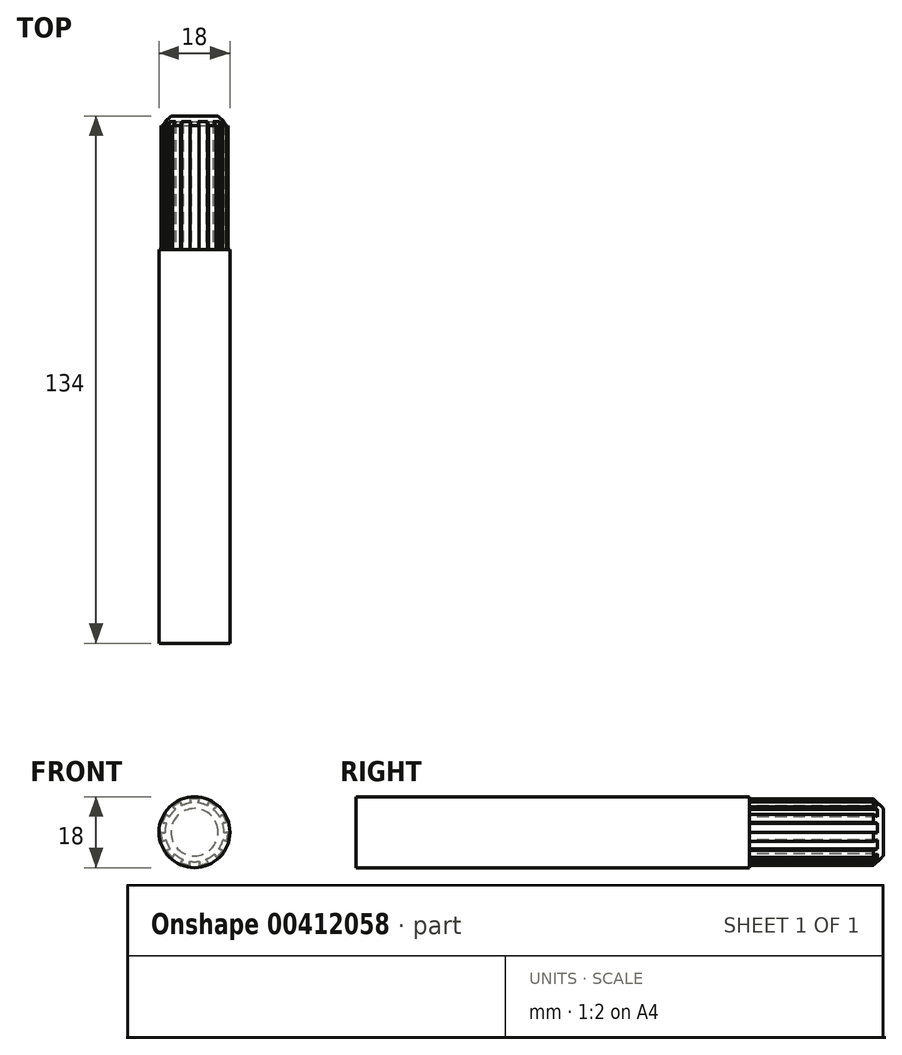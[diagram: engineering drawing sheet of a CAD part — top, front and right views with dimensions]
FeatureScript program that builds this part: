
annotation { "Feature Type Name" : "Feature", "Feature Type Description" : "" }
export const myFeature = defineFeature(function(context is Context, id is Id, definition is map)
    precondition{}
    {
        {
            var Q0;
            Q0=qCreatedBy(makeId("Front.planeOp"),FACE);
            var sketch = newSketch(context, id + "F0", { "sketchPlane" : qUnion([Q0])});
            skCircle(sketch, "E0", {"center": v(0, 0) * mm, "radius": 9 * mm});
            skSolve(sketch);
        }
        {
            var Q0;
            Q0=makeQuery(id+"F0.imprint","IMPRINT",FACE,{"disambiguationData":[TD([[makeQuery(id+"F0.imprint","IMPRINT",EDGE,{"derivedFrom":sQuery(id+"F0.wireOp",EDGE,"E0")}),1.0]])]});
            extrude(context, id + "F1", {"entities" : qUnion([Q0]), "depth" : 100 * mm});
        }
        {
            var Q0;
            Q0=qCreatedBy(makeId("Front.planeOp"),FACE);
            var sketch = newSketch(context, id + "F2", { "sketchPlane" : qUnion([Q0])});
            skCircle(sketch, "E1", {"center": v(0, 0) * mm, "radius": 8.5 * mm});
            skCircle(sketch, "E2", {"center": v(0, 0) * mm, "radius": 7.5 * mm});
            skLineSegment(sketch, "E3", {"start": v(0, 14.32) * mm, "end": v(0, -11.4) * mm, "construction": true});
            skPoint(sketch, "E4", {"position": v(-0.88, 7.45) * mm});
            skPoint(sketch, "E5", {"position": v(0.88, 7.45) * mm});
            skPoint(sketch, "E6", {"position": v(-1.17, 8.42) * mm});
            skPoint(sketch, "E7", {"position": v(1.17, 8.42) * mm});
            skLineSegment(sketch, "E8", {"start": v(0.88, 7.45) * mm, "end": v(1.17, 8.42) * mm});
            skLineSegment(sketch, "E9", {"start": v(-0.88, 7.45) * mm, "end": v(-1.17, 8.42) * mm});
            skPoint(sketch, "E10.1.0", {"position": v(-3.28, 6.74) * mm});
            skPoint(sketch, "E10.1.1", {"position": v(-5.54, 6.45) * mm});
            skLineSegment(sketch, "E10.1.2", {"start": v(-3.28, 6.74) * mm, "end": v(-3.57, 7.71) * mm});
            skPoint(sketch, "E10.1.3", {"position": v(-3.57, 7.71) * mm});
            skPoint(sketch, "E10.1.4", {"position": v(-4.77, 5.79) * mm});
            skLineSegment(sketch, "E10.1.5", {"start": v(-4.77, 5.79) * mm, "end": v(-5.54, 6.45) * mm});
            skPoint(sketch, "E10.2.0", {"position": v(-6.4, 3.9) * mm});
            skPoint(sketch, "E10.2.1", {"position": v(-8.14, 2.43) * mm});
            skLineSegment(sketch, "E10.2.2", {"start": v(-6.4, 3.9) * mm, "end": v(-7.17, 4.56) * mm});
            skPoint(sketch, "E10.2.3", {"position": v(-7.17, 4.56) * mm});
            skPoint(sketch, "E10.2.4", {"position": v(-7.14, 2.29) * mm});
            skLineSegment(sketch, "E10.2.5", {"start": v(-7.14, 2.29) * mm, "end": v(-8.14, 2.43) * mm});
            skPoint(sketch, "E10.3.0", {"position": v(-7.5, -0.18) * mm});
            skPoint(sketch, "E10.3.1", {"position": v(-8.17, -2.36) * mm});
            skLineSegment(sketch, "E10.3.2", {"start": v(-7.5, -0.18) * mm, "end": v(-8.5, -0.04) * mm});
            skPoint(sketch, "E10.3.3", {"position": v(-8.5, -0.04) * mm});
            skPoint(sketch, "E10.3.4", {"position": v(-7.25, -1.93) * mm});
            skLineSegment(sketch, "E10.3.5", {"start": v(-7.25, -1.93) * mm, "end": v(-8.17, -2.36) * mm});
            skPoint(sketch, "E10.4.0", {"position": v(-6.2, -4.2) * mm});
            skPoint(sketch, "E10.4.1", {"position": v(-5.6, -6.4) * mm});
            skLineSegment(sketch, "E10.4.2", {"start": v(-6.2, -4.2) * mm, "end": v(-7.13, -4.63) * mm});
            skPoint(sketch, "E10.4.3", {"position": v(-7.13, -4.63) * mm});
            skPoint(sketch, "E10.4.4", {"position": v(-5.05, -5.55) * mm});
            skLineSegment(sketch, "E10.4.5", {"start": v(-5.05, -5.55) * mm, "end": v(-5.6, -6.4) * mm});
            skPoint(sketch, "E10.5.0", {"position": v(-2.95, -6.9) * mm});
            skPoint(sketch, "E10.5.1", {"position": v(-1.25, -8.4) * mm});
            skLineSegment(sketch, "E10.5.2", {"start": v(-2.95, -6.9) * mm, "end": v(-3.5, -7.75) * mm});
            skPoint(sketch, "E10.5.3", {"position": v(-3.5, -7.75) * mm});
            skPoint(sketch, "E10.5.4", {"position": v(-1.25, -7.4) * mm});
            skLineSegment(sketch, "E10.5.5", {"start": v(-1.25, -7.4) * mm, "end": v(-1.25, -8.4) * mm});
            skPoint(sketch, "E10.6.0", {"position": v(1.25, -7.4) * mm});
            skPoint(sketch, "E10.6.1", {"position": v(3.5, -7.75) * mm});
            skLineSegment(sketch, "E10.6.2", {"start": v(1.25, -7.4) * mm, "end": v(1.25, -8.4) * mm});
            skPoint(sketch, "E10.6.3", {"position": v(1.25, -8.4) * mm});
            skPoint(sketch, "E10.6.4", {"position": v(2.95, -6.9) * mm});
            skLineSegment(sketch, "E10.6.5", {"start": v(2.95, -6.9) * mm, "end": v(3.5, -7.75) * mm});
            skPoint(sketch, "E10.7.0", {"position": v(5.05, -5.55) * mm});
            skPoint(sketch, "E10.7.1", {"position": v(7.13, -4.63) * mm});
            skLineSegment(sketch, "E10.7.2", {"start": v(5.05, -5.55) * mm, "end": v(5.6, -6.4) * mm});
            skPoint(sketch, "E10.7.3", {"position": v(5.6, -6.4) * mm});
            skPoint(sketch, "E10.7.4", {"position": v(6.2, -4.2) * mm});
            skLineSegment(sketch, "E10.7.5", {"start": v(6.2, -4.2) * mm, "end": v(7.13, -4.63) * mm});
            skPoint(sketch, "E10.8.0", {"position": v(7.25, -1.93) * mm});
            skPoint(sketch, "E10.8.1", {"position": v(8.5, -0.04) * mm});
            skLineSegment(sketch, "E10.8.2", {"start": v(7.25, -1.93) * mm, "end": v(8.17, -2.36) * mm});
            skPoint(sketch, "E10.8.3", {"position": v(8.17, -2.36) * mm});
            skPoint(sketch, "E10.8.4", {"position": v(7.5, -0.18) * mm});
            skLineSegment(sketch, "E10.8.5", {"start": v(7.5, -0.18) * mm, "end": v(8.5, -0.04) * mm});
            skPoint(sketch, "E10.9.0", {"position": v(7.14, 2.29) * mm});
            skPoint(sketch, "E10.9.1", {"position": v(7.17, 4.56) * mm});
            skLineSegment(sketch, "E10.9.2", {"start": v(7.14, 2.29) * mm, "end": v(8.14, 2.43) * mm});
            skPoint(sketch, "E10.9.3", {"position": v(8.14, 2.43) * mm});
            skPoint(sketch, "E10.9.4", {"position": v(6.4, 3.9) * mm});
            skLineSegment(sketch, "E10.9.5", {"start": v(6.4, 3.9) * mm, "end": v(7.17, 4.56) * mm});
            skPoint(sketch, "E10.10.0", {"position": v(4.77, 5.79) * mm});
            skPoint(sketch, "E10.10.1", {"position": v(3.57, 7.71) * mm});
            skLineSegment(sketch, "E10.10.2", {"start": v(4.77, 5.79) * mm, "end": v(5.54, 6.45) * mm});
            skPoint(sketch, "E10.10.3", {"position": v(5.54, 6.45) * mm});
            skPoint(sketch, "E10.10.4", {"position": v(3.28, 6.74) * mm});
            skLineSegment(sketch, "E10.10.5", {"start": v(3.28, 6.74) * mm, "end": v(3.57, 7.71) * mm});
            skSolve(sketch);
        }
        {
            var Q0;
            Q0 = qSketchRegion(id + "F2", true);
            var Q1;
            {var subQ0=sQuery(id+"F2.wireOp",EDGE,"E2");var subQ8=makeQuery(id+"F2.imprint","INTERSECT",VERTEX,{"derivedFrom":[subQ0,sQuery(id+"F2.wireOp",EDGE,"E10.9.2")]});Q1=makeQuery(id+"F2.imprint","IMPRINT",FACE,{"disambiguationData":[TD([[makeQuery(id+"F2.imprint","IMPRINT",EDGE,{"disambiguationData":[TD([[subQ8,-1.0]])],"derivedFrom":subQ0}),1.0]])]});}
            extrude(context, id + "F3", {"entities" : qUnion([Q0, Q1]), "operationType" : NewBodyOperationType.ADD, "oppositeDirection" : true, "depth" : 34 * mm});
        }
        {
            var Q0;
            Q0=makeQuery(id+"F3.opExtrude","CAP_EDGE",EDGE,{"disambiguationData":[OSD([sQuery(id+"F2.wireOp",EDGE,"E1")])],"isStart":false});
            chamfer(context, id + "F4", {"entities" : qUnion([Q0]), "width" : 2.5 * mm, "tangentPropagation" : true});
        }
        {
            var Q0;
            {var subQ0=sQuery(id+"F2.wireOp",EDGE,"E10.4.5");Q0=makeQuery(id+"F2.imprint","IMPRINT",FACE,{"disambiguationData":[TD([[makeQuery(id+"F2.imprint","IMPRINT",EDGE,{"derivedFrom":subQ0}),1.0]])]});}
            var Q1;
            {var subQ0=sQuery(id+"F2.wireOp",EDGE,"E10.3.5");Q1=makeQuery(id+"F2.imprint","IMPRINT",FACE,{"disambiguationData":[TD([[makeQuery(id+"F2.imprint","IMPRINT",EDGE,{"derivedFrom":subQ0}),1.0]])]});}
            var Q2;
            {var subQ0=sQuery(id+"F2.wireOp",EDGE,"E10.2.5");Q2=makeQuery(id+"F2.imprint","IMPRINT",FACE,{"disambiguationData":[TD([[makeQuery(id+"F2.imprint","IMPRINT",EDGE,{"derivedFrom":subQ0}),1.0]])]});}
            var Q3;
            {var subQ0=sQuery(id+"F2.wireOp",EDGE,"E10.1.5");Q3=makeQuery(id+"F2.imprint","IMPRINT",FACE,{"disambiguationData":[TD([[makeQuery(id+"F2.imprint","IMPRINT",EDGE,{"derivedFrom":subQ0}),1.0]])]});}
            var Q4;
            {var subQ0=sQuery(id+"F2.wireOp",EDGE,"E9");Q4=makeQuery(id+"F2.imprint","IMPRINT",FACE,{"disambiguationData":[TD([[makeQuery(id+"F2.imprint","IMPRINT",EDGE,{"derivedFrom":subQ0}),1.0]])]});}
            var Q5;
            {var subQ0=sQuery(id+"F2.wireOp",EDGE,"E8");Q5=makeQuery(id+"F2.imprint","IMPRINT",FACE,{"disambiguationData":[TD([[makeQuery(id+"F2.imprint","IMPRINT",EDGE,{"derivedFrom":subQ0}),-1.0]])]});}
            var Q6;
            {var subQ0=sQuery(id+"F2.wireOp",EDGE,"E10.9.5");Q6=makeQuery(id+"F2.imprint","IMPRINT",FACE,{"disambiguationData":[TD([[makeQuery(id+"F2.imprint","IMPRINT",EDGE,{"derivedFrom":subQ0}),1.0]])]});}
            var Q7;
            {var subQ0=sQuery(id+"F2.wireOp",EDGE,"E10.8.5");Q7=makeQuery(id+"F2.imprint","IMPRINT",FACE,{"disambiguationData":[TD([[makeQuery(id+"F2.imprint","IMPRINT",EDGE,{"derivedFrom":subQ0}),1.0]])]});}
            var Q8;
            {var subQ0=sQuery(id+"F2.wireOp",EDGE,"E10.7.5");Q8=makeQuery(id+"F2.imprint","IMPRINT",FACE,{"disambiguationData":[TD([[makeQuery(id+"F2.imprint","IMPRINT",EDGE,{"derivedFrom":subQ0}),1.0]])]});}
            var Q9;
            {var subQ0=sQuery(id+"F2.wireOp",EDGE,"E10.6.5");Q9=makeQuery(id+"F2.imprint","IMPRINT",FACE,{"disambiguationData":[TD([[makeQuery(id+"F2.imprint","IMPRINT",EDGE,{"derivedFrom":subQ0}),1.0]])]});}
            var Q10;
            {var subQ0=sQuery(id+"F2.wireOp",EDGE,"E10.5.5");Q10=makeQuery(id+"F2.imprint","IMPRINT",FACE,{"disambiguationData":[TD([[makeQuery(id+"F2.imprint","IMPRINT",EDGE,{"derivedFrom":subQ0}),1.0]])]});}
            extrude(context, id + "F5", {"entities" : qUnion([Q0, Q1, Q2, Q3, Q4, Q5, Q6, Q7, Q8, Q9, Q10]), "operationType" : NewBodyOperationType.REMOVE, "oppositeDirection" : true, "depth" : 34 * mm});
        }
    });
